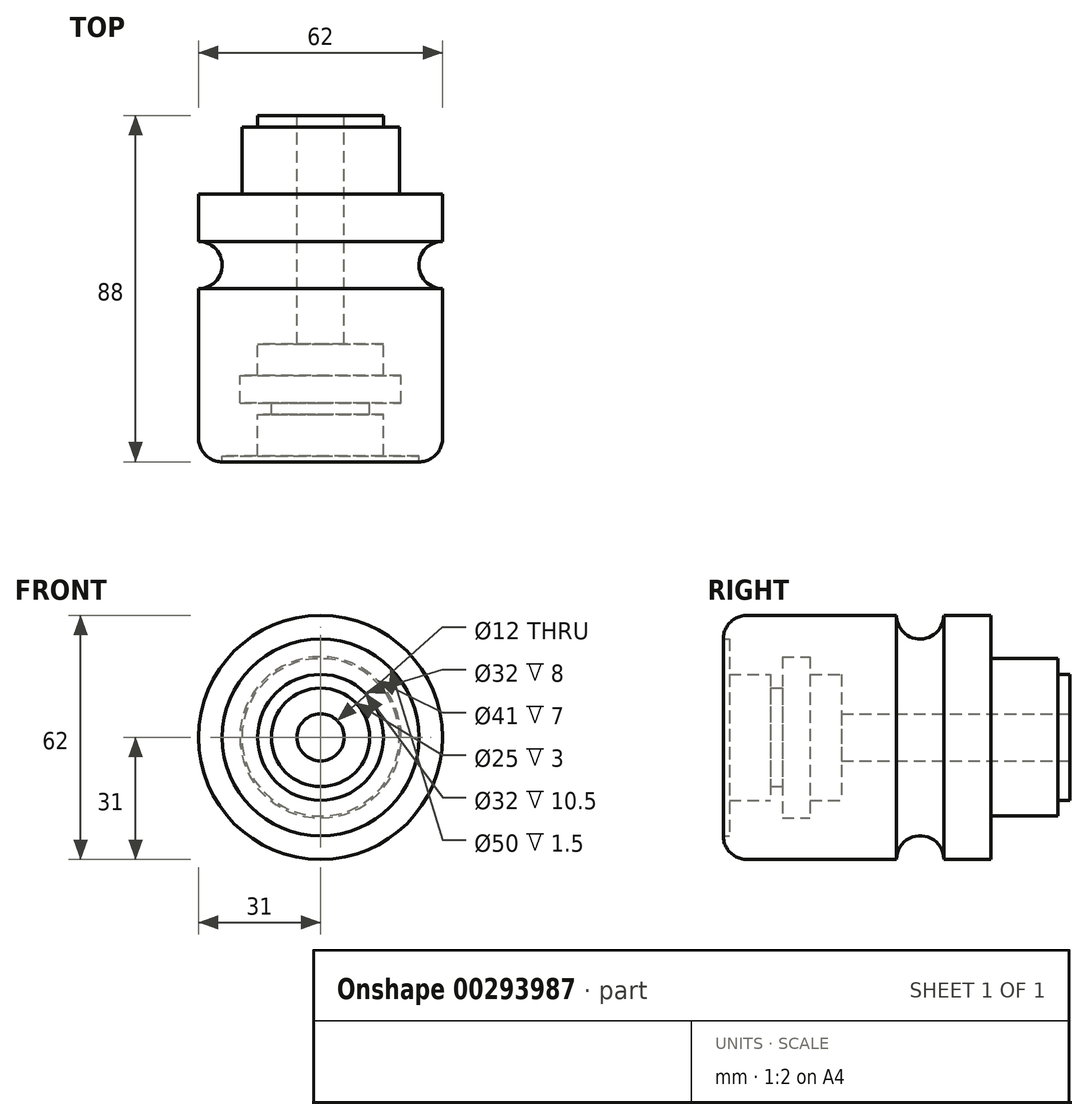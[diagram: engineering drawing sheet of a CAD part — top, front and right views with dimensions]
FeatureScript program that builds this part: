
annotation { "Feature Type Name" : "Feature", "Feature Type Description" : "" }
export const myFeature = defineFeature(function(context is Context, id is Id, definition is map)
    precondition{}
    {
        {
            var Q0;
            Q0=qCreatedBy(makeId("Right.planeOp"),FACE);
            var sketch = newSketch(context, id + "F0", { "sketchPlane" : qUnion([Q0])});
            skLineSegment(sketch, "E0", {"start": v(0, 0) * mm, "end": v(0, 25) * mm});
            skLineSegment(sketch, "E1", {"start": v(6, 31) * mm, "end": v(44, 31) * mm});
            skLineSegment(sketch, "E2", {"start": v(56, 31) * mm, "end": v(68, 31) * mm});
            skLineSegment(sketch, "E3", {"start": v(68, 31) * mm, "end": v(68, 20) * mm});
            skLineSegment(sketch, "E4", {"start": v(68, 20) * mm, "end": v(85, 20) * mm});
            skLineSegment(sketch, "E5", {"start": v(85, 20) * mm, "end": v(85, 16) * mm});
            skLineSegment(sketch, "E6", {"start": v(85, 16) * mm, "end": v(88, 16) * mm});
            skLineSegment(sketch, "E7", {"start": v(88, 16) * mm, "end": v(88, 0) * mm});
            skLineSegment(sketch, "E8", {"start": v(0, 0) * mm, "end": v(88, 0) * mm});
            skArc(sketch, "E9", {"start": v(44, 31) * mm, "mid": v(50, 25) * mm, "end": v(56, 31) * mm});
            skArc(sketch, "E10", {"start": v(6, 31) * mm, "mid": v(1.76, 29.24) * mm, "end": v(0, 25) * mm});
            skLineSegment(sketch, "E11", {"start": v(-13.56, 0) * mm, "end": v(99.76, 0) * mm, "construction": true});
            skPoint(sketch, "E11.endSnap0", {"position": v(44, 0) * mm});
            skSolve(sketch);
        }
        {
            var Q0;
            Q0 = qSketchRegion(id + "F0", true);
            var Q1;
            Q1=sQuery(id+"F0.wireOp",EDGE,"E11");
            revolve(context, id + "F1", {"entities" : qUnion([Q0]), "axis" : qUnion([Q1]), "revolveType" : RevolveType.FULL});
        }
        {
            var Q0;
            Q0=qCreatedBy(makeId("Right.planeOp"),FACE);
            var sketch = newSketch(context, id + "F2", { "sketchPlane" : qUnion([Q0])});
            skLineSegment(sketch, "E12", {"start": v(0, 0) * mm, "end": v(0, 25) * mm});
            skLineSegment(sketch, "E13", {"start": v(0, 25) * mm, "end": v(1.5, 25) * mm});
            skLineSegment(sketch, "E14", {"start": v(1.5, 25) * mm, "end": v(1.5, 16) * mm});
            skLineSegment(sketch, "E15", {"start": v(1.5, 16) * mm, "end": v(12, 16) * mm});
            skLineSegment(sketch, "E16", {"start": v(12, 16) * mm, "end": v(12, 12.5) * mm});
            skLineSegment(sketch, "E17", {"start": v(12, 12.5) * mm, "end": v(15, 12.5) * mm});
            skLineSegment(sketch, "E18", {"start": v(15, 12.5) * mm, "end": v(15, 20.5) * mm});
            skLineSegment(sketch, "E19", {"start": v(15, 20.5) * mm, "end": v(22, 20.5) * mm});
            skLineSegment(sketch, "E20", {"start": v(22, 20.5) * mm, "end": v(22, 16) * mm});
            skLineSegment(sketch, "E21", {"start": v(22, 16) * mm, "end": v(30, 16) * mm});
            skLineSegment(sketch, "E22", {"start": v(30, 16) * mm, "end": v(30, 6) * mm});
            skLineSegment(sketch, "E23", {"start": v(30, 6) * mm, "end": v(88, 6) * mm});
            skLineSegment(sketch, "E24", {"start": v(88, 6) * mm, "end": v(88, 0) * mm});
            skLineSegment(sketch, "E25", {"start": v(88, 0) * mm, "end": v(0, 0) * mm});
            skSolve(sketch);
        }
        {
            var Q0;
            Q0=qCreatedBy(makeId("Right.planeOp"),FACE);
            var sketch = newSketch(context, id + "F3", { "sketchPlane" : qUnion([Q0])});
            skLineSegment(sketch, "E26", {"start": v(-15.46, 0) * mm, "end": v(96.13, 0) * mm, "construction": true});
            skSolve(sketch);
        }
        {
            var Q0;
            Q0=makeQuery(id+"F2.imprint","IMPRINT",FACE,{"disambiguationData":[TD([[makeQuery(id+"F2.imprint","IMPRINT",EDGE,{"derivedFrom":sQuery(id+"F2.wireOp",EDGE,"E12")}),-1.0]])]});
            var Q1;
            Q1=sQuery(id+"F3.wireOp",EDGE,"E26");
            revolve(context, id + "F4", {"operationType" : NewBodyOperationType.REMOVE, "entities" : qUnion([Q0]), "axis" : qUnion([Q1]), "revolveType" : RevolveType.FULL, "oppositeDirection" : true});
        }
    });
